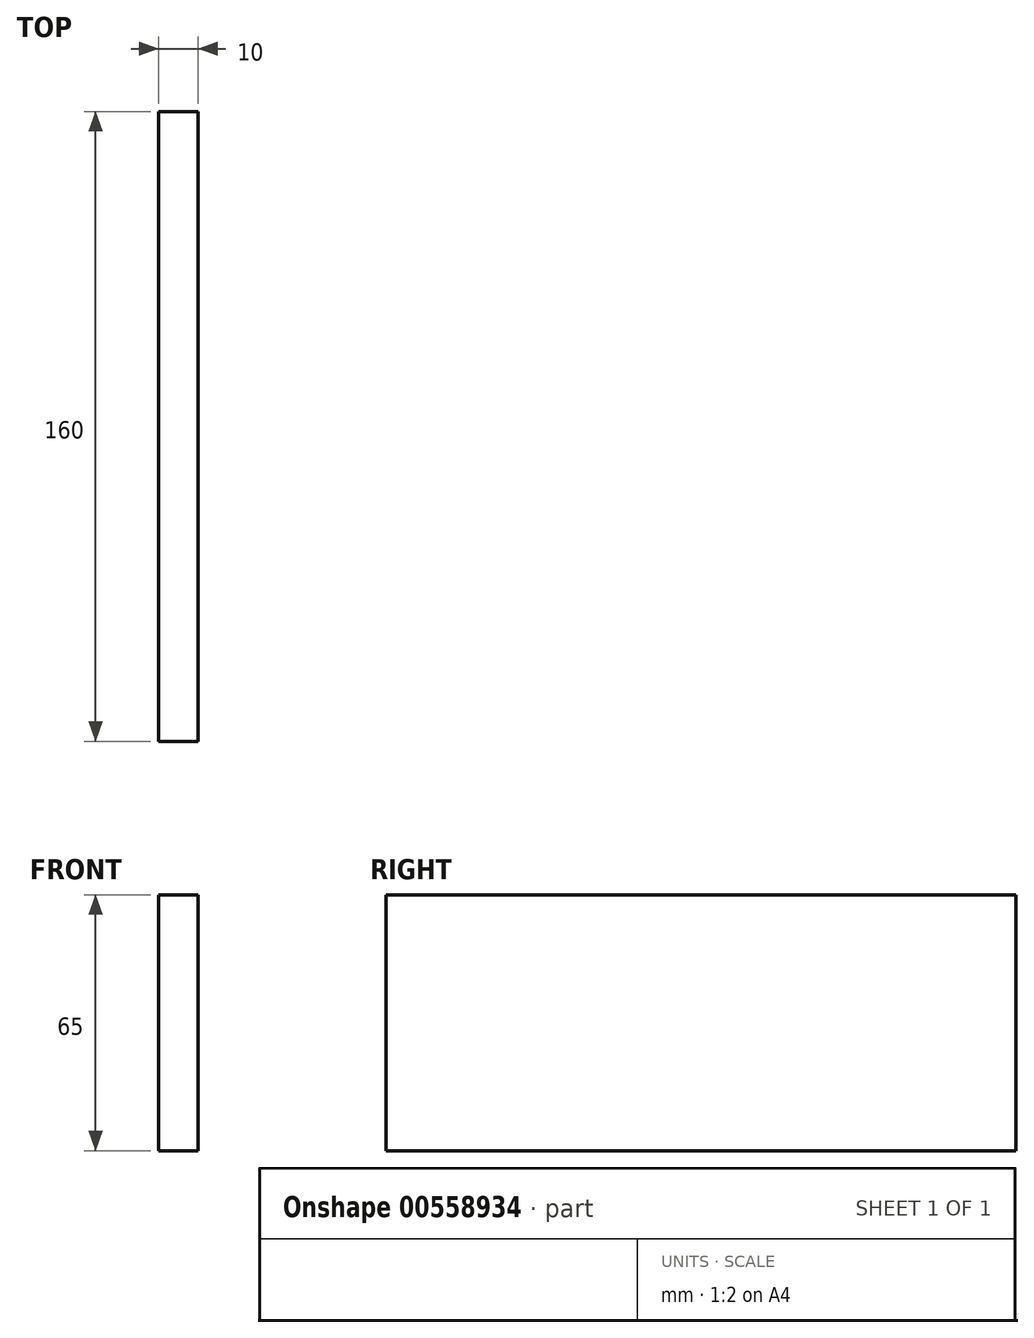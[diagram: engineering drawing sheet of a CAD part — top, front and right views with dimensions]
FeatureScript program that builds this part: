
annotation { "Feature Type Name" : "Feature", "Feature Type Description" : "" }
export const myFeature = defineFeature(function(context is Context, id is Id, definition is map)
    precondition{}
    {
        {
            var Q0;
            Q0=qCreatedBy(makeId("Right.planeOp"),FACE);
            var sketch = newSketch(context, id + "F0", { "sketchPlane" : qUnion([Q0])});
            skLineSegment(sketch, "E0.bottom", {"start": v(80, -32.5) * mm, "end": v(-80, -32.5) * mm});
            skLineSegment(sketch, "E0.top", {"start": v(80, 32.5) * mm, "end": v(-80, 32.5) * mm});
            skLineSegment(sketch, "E0.left", {"start": v(80, -32.5) * mm, "end": v(80, 32.5) * mm});
            skLineSegment(sketch, "E0.right", {"start": v(-80, -32.5) * mm, "end": v(-80, 32.5) * mm});
            skPoint(sketch, "E0.middle", {"position": v(0, 0) * mm});
            skSolve(sketch);
        }
        {
            var Q0;
            Q0 = qSketchRegion(id + "F0", true);
            extrude(context, id + "F1", {"entities" : qUnion([Q0]), "depth" : 10 * mm, "offsetDistance" : 25 * mm});
        }
    });
